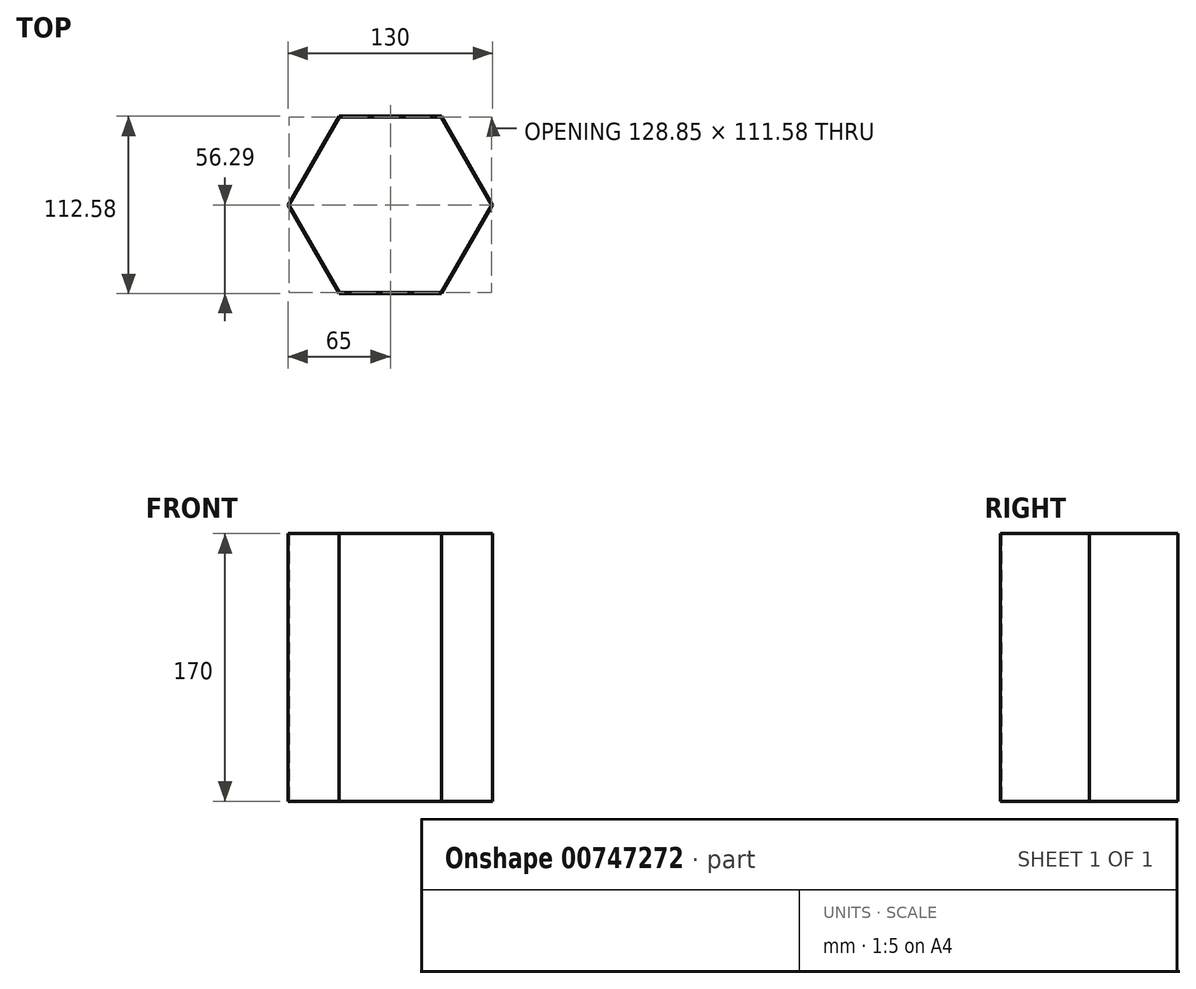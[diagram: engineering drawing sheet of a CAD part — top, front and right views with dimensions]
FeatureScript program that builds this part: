
annotation { "Feature Type Name" : "Feature", "Feature Type Description" : "" }
export const myFeature = defineFeature(function(context is Context, id is Id, definition is map)
    precondition{}
    {
        {
            var Q0;
            Q0=qCreatedBy(makeId("Top.planeOp"),FACE);
            var sketch = newSketch(context, id + "F0", { "sketchPlane" : qUnion([Q0])});
            skCircle(sketch, "E0.cCircle", {"center": v(0, 0) * mm, "radius": 56.3 * mm, "construction": true});
            skLineSegment(sketch, "E0.0", {"start": v(32.5, 56.3) * mm, "end": v(65, 0) * mm});
            skLineSegment(sketch, "E0.1", {"start": v(65, 0) * mm, "end": v(32.5, -56.3) * mm});
            skLineSegment(sketch, "E0.2", {"start": v(32.5, -56.3) * mm, "end": v(-32.5, -56.3) * mm});
            skLineSegment(sketch, "E0.3", {"start": v(-32.5, -56.3) * mm, "end": v(-65, 0) * mm});
            skLineSegment(sketch, "E0.4", {"start": v(-65, 0) * mm, "end": v(-32.5, 56.3) * mm});
            skLineSegment(sketch, "E0.5", {"start": v(-32.5, 56.3) * mm, "end": v(32.5, 56.3) * mm});
            skPoint(sketch, "E0.0.midPoint", {"position": v(48.75, 28.15) * mm});
            skCircle(sketch, "E1.cCircle", {"center": v(0, 0) * mm, "radius": 55.8 * mm, "construction": true});
            skLineSegment(sketch, "E1.0", {"start": v(64.42, 0) * mm, "end": v(32.21, -55.8) * mm});
            skLineSegment(sketch, "E1.1", {"start": v(32.21, -55.8) * mm, "end": v(-32.21, -55.8) * mm});
            skLineSegment(sketch, "E1.2", {"start": v(-32.21, -55.8) * mm, "end": v(-64.42, 0) * mm});
            skLineSegment(sketch, "E1.3", {"start": v(-64.42, 0) * mm, "end": v(-32.21, 55.8) * mm});
            skLineSegment(sketch, "E1.4", {"start": v(-32.21, 55.8) * mm, "end": v(32.21, 55.8) * mm});
            skLineSegment(sketch, "E1.5", {"start": v(32.21, 55.8) * mm, "end": v(64.42, 0) * mm});
            skPoint(sketch, "E1.0.midPoint", {"position": v(48.32, -27.9) * mm});
            skSolve(sketch);
        }
        {
            var Q0;
            Q0=qSketchRegion(id+"F0",true);
            extrude(context, id + "F1", {"entities" : qUnion([Q0]), "depth" : 170 * mm, "offsetDistance" : 25 * mm});
        }
    });
